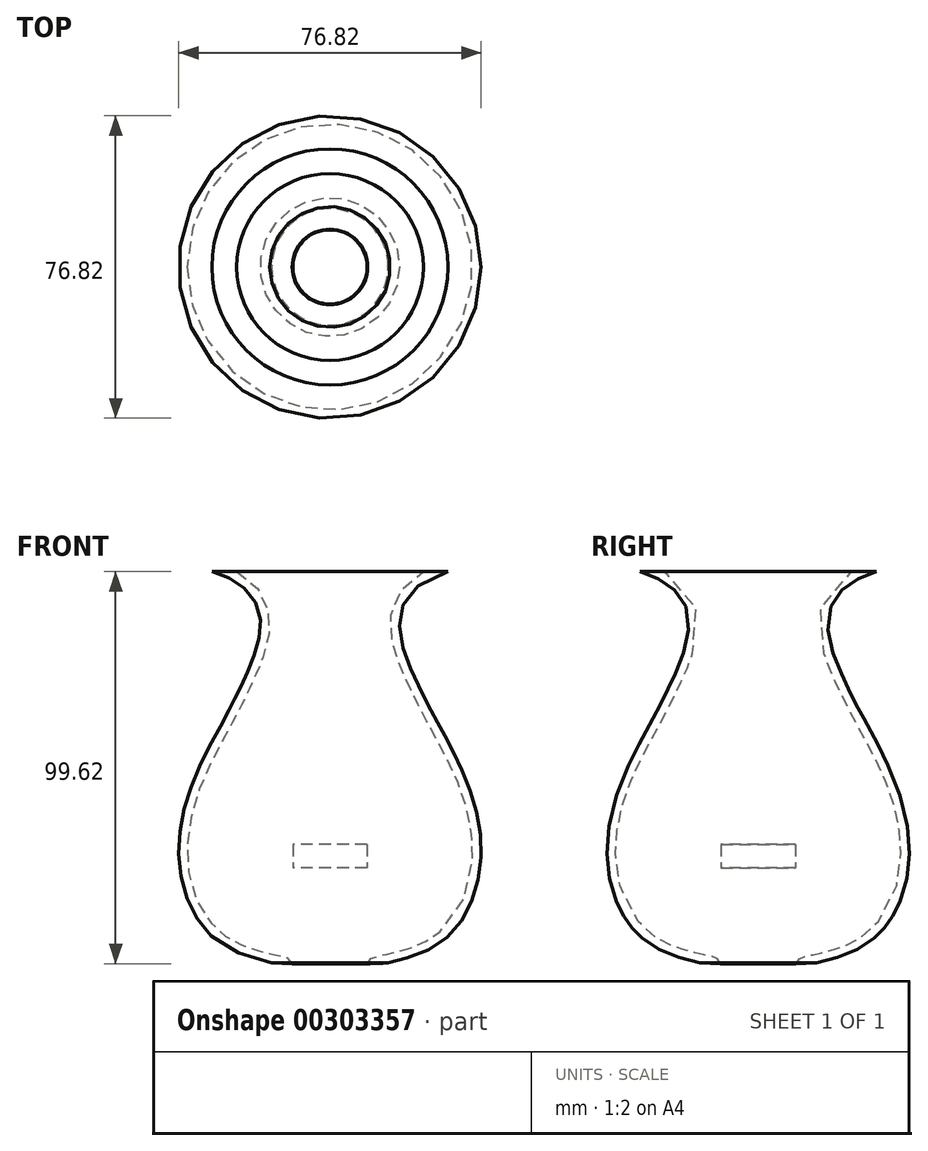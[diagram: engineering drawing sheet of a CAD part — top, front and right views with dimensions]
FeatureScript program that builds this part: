
annotation { "Feature Type Name" : "Feature", "Feature Type Description" : "" }
export const myFeature = defineFeature(function(context is Context, id is Id, definition is map)
    precondition{}
    {
        {
            var Q0;
            Q0=qCreatedBy(makeId("Front.planeOp"),FACE);
            var sketch = newSketch(context, id + "F0", { "sketchPlane" : qUnion([Q0])});
            skFitSpline(sketch, "E0", {"points": [v(30, 75.3) * mm, v(21.52, 48.52) * mm, v(28.09, 35.58) * mm, v(38.18, 8.65) * mm, v(26.25, -20.12) * mm, v(12.12, -24.95) * mm, v(39.9, -24.9) * mm], "startDerivative": vector(-296.12, -88.24) * mm, "endDerivative": vector(-9.6, -0.96) * mm});
            skLineSegment(sketch, "E1", {"start": v(30, 75.3) * mm, "end": v(0, 75.3) * mm});
            skLineSegment(sketch, "E2", {"start": v(0, 75.3) * mm, "end": v(0, -24.7) * mm});
            skFitSpline(sketch, "E3.trimOffspring", {"points": [v(30, 75.3) * mm, v(21.52, 48.52) * mm, v(28.09, 35.58) * mm, v(38.18, 8.65) * mm, v(26.25, -20.12) * mm, v(12.12, -24.95) * mm, v(39.9, -24.9) * mm], "startDerivative": vector(-296.12, -88.24) * mm, "endDerivative": vector(-9.6, -0.96) * mm});
            skLineSegment(sketch, "E4.trimOffspring", {"start": v(14.79, -24.11) * mm, "end": v(0, -24.7) * mm});
            skFitSpline(sketch, "E5", {"points": [v(29.36, 77.44) * mm, v(27.72, 76.95) * mm, v(24.76, 75.83) * mm, v(21.24, 73.73) * mm, v(18.56, 71.24) * mm, v(16.72, 68.42) * mm, v(15.68, 65.41) * mm, v(15.33, 62.37) * mm, v(15.51, 59.38) * mm, v(16.08, 56.5) * mm, v(16.92, 53.74) * mm, v(17.74, 51.58) * mm, v(18.42, 49.97) * mm, v(18.93, 48.82) * mm, v(19.42, 47.74) * mm, v(20.04, 46.4) * mm, v(20.76, 44.86) * mm, v(21.56, 43.2) * mm, v(22.32, 41.67) * mm, v(23.3, 39.74) * mm, v(24.28, 37.9) * mm, v(25.34, 35.94) * mm, v(26.2, 34.37) * mm, v(27.14, 32.66) * mm, v(28.47, 30.2) * mm, v(30.2, 26.84) * mm, v(32.22, 22.39) * mm, v(34.01, 17.61) * mm, v(35.16, 13.43) * mm, v(35.79, 10.02) * mm, v(36.19, 6.57) * mm, v(36.24, 2.2) * mm, v(35.55, -2.95) * mm, v(34.08, -7.78) * mm, v(32.2, -11.37) * mm, v(30.3, -13.91) * mm, v(28.67, -15.63) * mm, v(27.14, -16.9) * mm, v(25.8, -17.8) * mm, v(24.4, -18.62) * mm, v(22.45, -19.53) * mm, v(20.4, -20.28) * mm, v(18.78, -20.8) * mm, v(17.6, -21.13) * mm, v(16.45, -21.43) * mm, v(15.38, -21.7) * mm, v(14.55, -21.88) * mm, v(13.94, -22.01) * mm, v(13.51, -22.1) * mm, v(13.1, -22.2) * mm, v(12.74, -22.27) * mm, v(12.4, -22.35) * mm, v(12.08, -22.42) * mm, v(11.85, -22.47) * mm, v(11.67, -22.52) * mm, v(11.53, -22.55) * mm, v(11.4, -22.6) * mm, v(11.26, -22.63) * mm, v(11.1, -22.7) * mm, v(10.94, -22.76) * mm, v(10.77, -22.84) * mm, v(10.62, -22.93) * mm, v(10.42, -23.07) * mm, v(10.16, -23.3) * mm, v(9.9, -23.63) * mm, v(9.7, -24.04) * mm, v(9.59, -24.42) * mm, v(9.54, -24.87) * mm, v(9.6, -25.32) * mm, v(9.72, -25.74) * mm, v(9.97, -26.2) * mm, v(10.3, -26.56) * mm, v(10.63, -26.78) * mm, v(10.87, -26.91) * mm, v(11.06, -27) * mm, v(11.2, -27.04) * mm, v(11.37, -27.09) * mm, v(11.53, -27.12) * mm, v(11.7, -27.15) * mm, v(11.85, -27.17) * mm, v(12, -27.18) * mm, v(12.16, -27.2) * mm, v(12.33, -27.21) * mm, v(12.56, -27.23) * mm, v(12.87, -27.24) * mm, v(13.3, -27.26) * mm, v(13.77, -27.27) * mm, v(14.28, -27.29) * mm, v(15.02, -27.3) * mm, v(16.05, -27.31) * mm, v(17.42, -27.32) * mm, v(18.91, -27.32) * mm, v(20.5, -27.32) * mm, v(22.17, -27.31) * mm, v(24.45, -27.3) * mm, v(27.37, -27.27) * mm, v(30.79, -27.23) * mm, v(33.94, -27.2) * mm, v(36.63, -27.16) * mm, v(38.16, -27.14) * mm, v(38.91, -27.13) * mm, v(39.24, -27.12) * mm, v(39.5, -27.12) * mm, v(39.66, -27.12) * mm, v(39.76, -27.12) * mm, v(39.8, -27.12) * mm, v(39.81, -27.12) * mm, v(39.82, -27.12) * mm, v(39.82, -27.12) * mm, v(39.82, -27.12) * mm, v(39.83, -27.12) * mm, v(39.84, -27.12) * mm, v(39.87, -27.12) * mm, v(39.9, -27.12) * mm, v(39.95, -27.12) * mm, v(39.99, -27.12) * mm, v(40.01, -27.12) * mm]});
            skSolve(sketch);
        }
        {
            var Q0;
            {var subQ0=sQuery(id+"F0.wireOp",EDGE,"E0");Q0=makeQuery(id+"F0.imprint","IMPRINT",FACE,{"disambiguationData":[TD([[makeQuery(id+"F0.imprint","IMPRINT",EDGE,{"derivedFrom":subQ0}),-1.0]])]});}
            var Q1;
            {var subQ0=sQuery(id+"F0.wireOp",EDGE,"E2");Q1=makeQuery(id+"F0.imprint","IMPRINT",FACE,{"disambiguationData":[TD([[makeQuery(id+"F0.imprint","IMPRINT",EDGE,{"derivedFrom":subQ0}),1.0]])]});}
            var Q2;
            Q2=sQuery(id+"F0.wireOp",EDGE,"E2");
            revolve(context, id + "F1", {"entities" : qUnion([Q0, Q1]), "axis" : qUnion([Q2]), "revolveType" : RevolveType.FULL});
        }
        {
            var Q0;
            {var subQ0=sQuery(id+"F0.wireOp",EDGE,"E2");Q0=makeQuery(id+"F0.imprint","IMPRINT",FACE,{"disambiguationData":[TD([[makeQuery(id+"F0.imprint","IMPRINT",EDGE,{"derivedFrom":subQ0}),1.0]])]});}
            var Q1;
            Q1=sQuery(id+"F0.wireOp",EDGE,"E2");
            revolve(context, id + "F2", {"operationType" : NewBodyOperationType.REMOVE, "entities" : qUnion([Q0]), "axis" : qUnion([Q1]), "revolveType" : RevolveType.FULL, "oppositeDirection" : true});
        }
        {
            var Q0;
            Q0=qCreatedBy(makeId("Top.planeOp"),FACE);
            var sketch = newSketch(context, id + "F3", { "sketchPlane" : qUnion([Q0])});
            skCircle(sketch, "E6", {"center": v(0, 0) * mm, "radius": 9.43 * mm});
            skSolve(sketch);
        }
        {
            var Q0;
            Q0=makeQuery(id+"F3.imprint","IMPRINT",FACE,{"disambiguationData":[TD([[makeQuery(id+"F3.imprint","IMPRINT",EDGE,{"derivedFrom":sQuery(id+"F3.wireOp",EDGE,"E6")}),1.0]])]});
            extrude(context, id + "F4", {"entities" : qUnion([Q0]), "depth" : 6 * mm});
        }
    });
